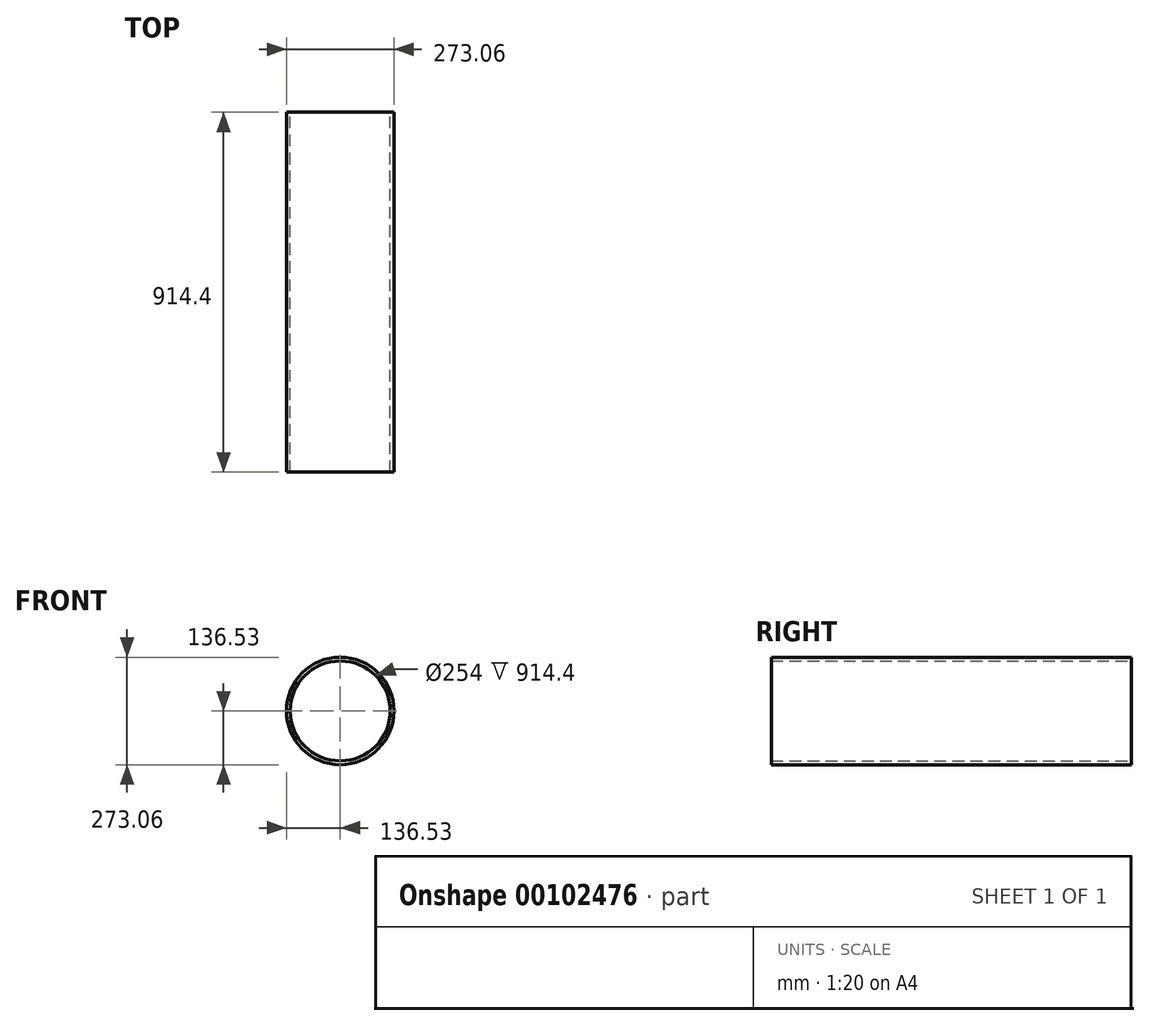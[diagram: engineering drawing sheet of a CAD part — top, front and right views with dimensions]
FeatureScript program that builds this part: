
annotation { "Feature Type Name" : "Feature", "Feature Type Description" : "" }
export const myFeature = defineFeature(function(context is Context, id is Id, definition is map)
    precondition{}
    {
        {
            var Q0;
            Q0=qCreatedBy(makeId("Front.planeOp"),FACE);
            var sketch = newSketch(context, id + "F0", { "sketchPlane" : qUnion([Q0])});
            skCircle(sketch, "E0", {"center": v(0, 0) * mm, "radius": 127 * mm});
            skCircle(sketch, "E1", {"center": v(0, 0) * mm, "radius": 136.53 * mm});
            skSolve(sketch);
        }
        {
            var Q0;
            Q0 = qSketchRegion(id + "F0", true);
            extrude(context, id + "F1", {"entities" : qUnion([Q0]), "depth" : 914.4 * mm});
        }
    });
